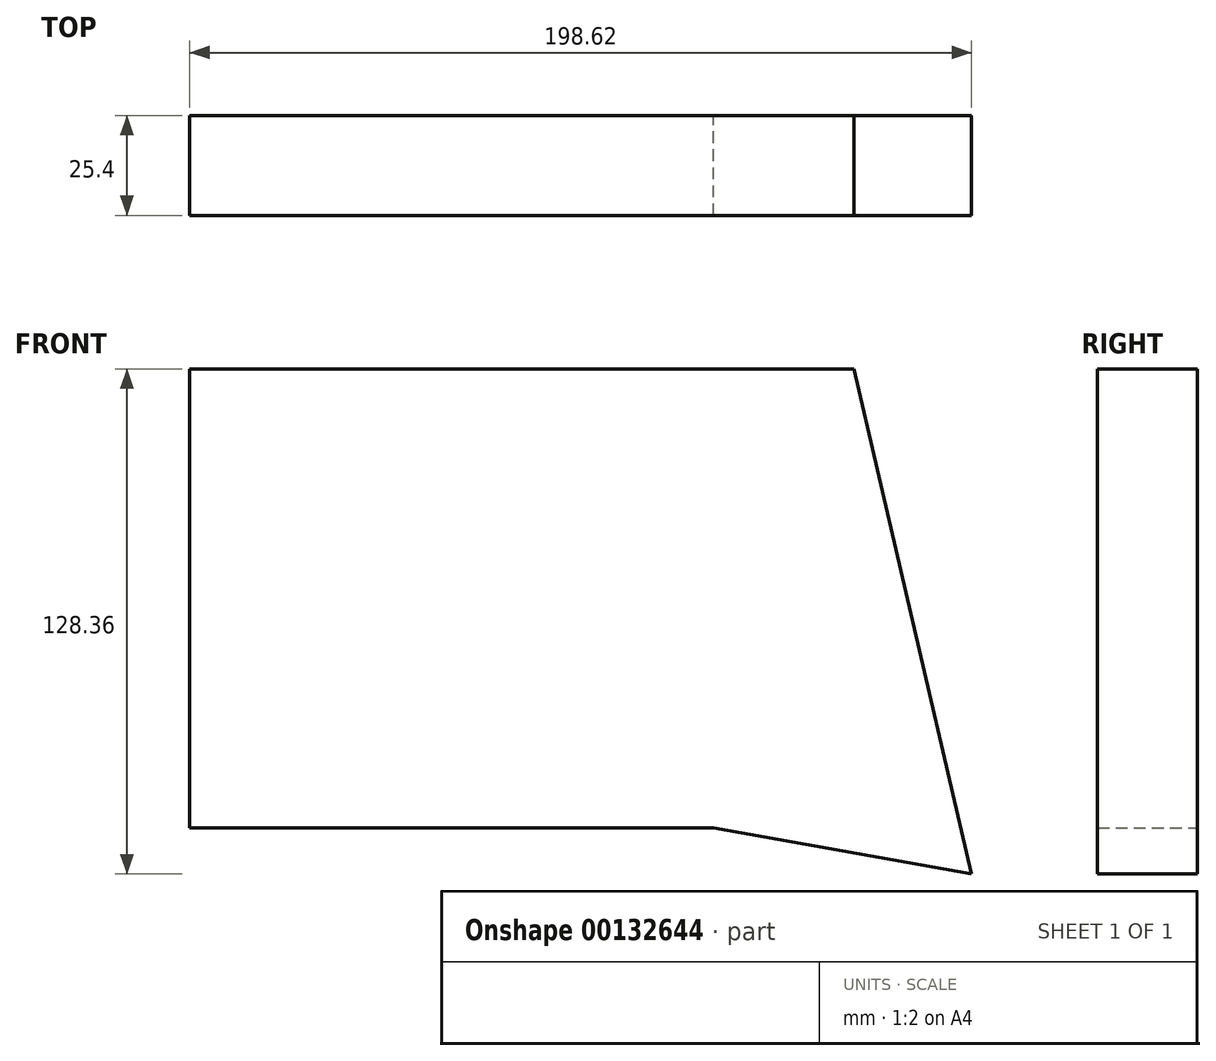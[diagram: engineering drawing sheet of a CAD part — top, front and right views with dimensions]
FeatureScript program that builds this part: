
annotation { "Feature Type Name" : "Feature", "Feature Type Description" : "" }
export const myFeature = defineFeature(function(context is Context, id is Id, definition is map)
    precondition{}
    {
        {
            var Q0;
            Q0=qCreatedBy(makeId("Front.planeOp"),FACE);
            var sketch = newSketch(context, id + "F0", { "sketchPlane" : qUnion([Q0])});
            skCircle(sketch, "E0.cCircle", {"center": v(64, 0) * mm, "radius": 52.1 * mm, "construction": true});
            skLineSegment(sketch, "E0.0", {"start": v(43.31, 70.7) * mm, "end": v(134.7, 20.7) * mm});
            skLineSegment(sketch, "E0.1", {"start": v(134.7, 20.7) * mm, "end": v(84.7, -70.7) * mm});
            skLineSegment(sketch, "E0.2", {"start": v(84.7, -70.7) * mm, "end": v(-6.7, -20.7) * mm});
            skLineSegment(sketch, "E0.3", {"start": v(-6.7, -20.7) * mm, "end": v(43.31, 70.7) * mm});
            skPoint(sketch, "E0.0.midPoint", {"position": v(89.01, 45.7) * mm});
            skCircle(sketch, "E1.cCircle", {"center": v(16, -114.4) * mm, "radius": 48.74 * mm, "construction": true});
            skLineSegment(sketch, "E1.0", {"start": v(-46.04, -84.36) * mm, "end": v(46.04, -52.35) * mm});
            skLineSegment(sketch, "E1.1", {"start": v(46.04, -52.35) * mm, "end": v(78.05, -144.44) * mm});
            skLineSegment(sketch, "E1.2", {"start": v(78.05, -144.44) * mm, "end": v(-14.04, -176.44) * mm});
            skLineSegment(sketch, "E1.3", {"start": v(-14.04, -176.44) * mm, "end": v(-46.04, -84.36) * mm});
            skPoint(sketch, "E1.0.midPoint", {"position": v(0, -68.35) * mm});
            skSolve(sketch);
        }
        {
            var Q0;
            Q0 = qBodyType(qCreatedBy(id + "F0" ,EDGE), BodyType.WIRE);
            extrude(context, id + "F1", {"bodyType" : ExtendedToolBodyType.SURFACE, "surfaceEntities" : qUnion([Q0]), "depth" : 109.1 * mm});
        }
        {
            var Q0;
            Q0=qCreatedBy(makeId("Front.planeOp"),FACE);
            var sketch = newSketch(context, id + "F2", { "sketchPlane" : qUnion([Q0])});
            skLineSegment(sketch, "E2", {"start": v(289.98, -81.57) * mm, "end": v(157, -81.57) * mm});
            skLineSegment(sketch, "E3", {"start": v(157, -81.57) * mm, "end": v(157, 35.02) * mm});
            skLineSegment(sketch, "E4", {"start": v(157, 35.02) * mm, "end": v(325.7, 35.02) * mm});
            skLineSegment(sketch, "E5", {"start": v(325.7, 35.02) * mm, "end": v(355.63, -93.34) * mm});
            skLineSegment(sketch, "E6", {"start": v(355.63, -93.34) * mm, "end": v(289.98, -81.57) * mm});
            skSolve(sketch);
        }
        {
            var Q0;
            Q0 = qSketchRegion(id + "F2", true);
            extrude(context, id + "F3", {"entities" : qUnion([Q0]), "depth" : 25.4 * mm});
        }
    });
